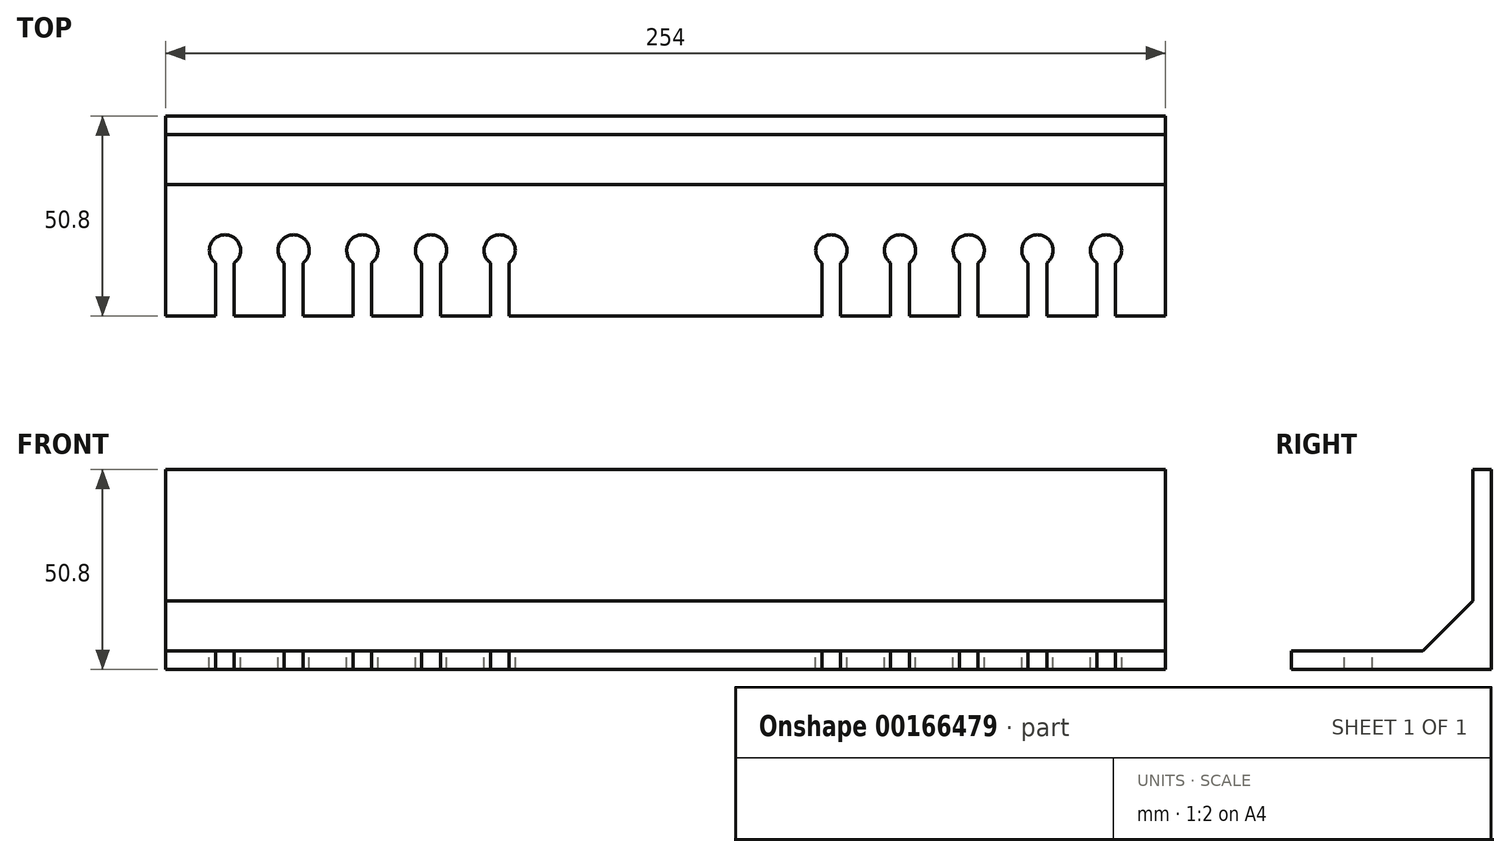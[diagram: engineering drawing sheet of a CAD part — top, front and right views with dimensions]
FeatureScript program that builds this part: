
annotation { "Feature Type Name" : "Feature", "Feature Type Description" : "" }
export const myFeature = defineFeature(function(context is Context, id is Id, definition is map)
    precondition{}
    {
        {
            var Q0;
            Q0=qCreatedBy(makeId("Right.planeOp"),FACE);
            var sketch = newSketch(context, id + "F0", { "sketchPlane" : qUnion([Q0])});
            skLineSegment(sketch, "E0.top", {"start": v(0, 46.05) * mm, "end": v(4.75, 46.05) * mm});
            skLineSegment(sketch, "E1.top", {"start": v(4.75, -4.75) * mm, "end": v(-46.05, -4.75) * mm});
            skLineSegment(sketch, "E1.right", {"start": v(-46.05, 0) * mm, "end": v(-46.05, -4.75) * mm});
            skLineSegment(sketch, "E2.trimOffspring", {"start": v(-12.7, 0) * mm, "end": v(-46.05, 0) * mm});
            skPoint(sketch, "E0.bottom.start.orphan", {"position": v(0, 0) * mm});
            skLineSegment(sketch, "E3", {"start": v(0, 46.05) * mm, "end": v(0, 12.7) * mm});
            skLineSegment(sketch, "E4", {"start": v(-12.7, 0) * mm, "end": v(0, 12.7) * mm});
            skLineSegment(sketch, "E5", {"start": v(4.75, 46.05) * mm, "end": v(4.75, -4.75) * mm});
            skSolve(sketch);
        }
        {
            var Q0;
            Q0 = qSketchRegion(id + "F0", true);
            extrude(context, id + "F1", {"entities" : qUnion([Q0]), "depth" : 254 * mm});
        }
        {
            var Q0;
            Q0=makeQuery(id+"F1.opExtrude","SWEPT_FACE",FACE,{"disambiguationData":[OSD([sQuery(id+"F0.wireOp",EDGE,"E2.trimOffspring")])]});
            var sketch = newSketch(context, id + "F2", { "sketchPlane" : qUnion([Q0])});
            skLineSegment(sketch, "E6.bottom", {"start": v(12.7, -46.05) * mm, "end": v(17.45, -46.05) * mm});
            skLineSegment(sketch, "E6.left", {"start": v(12.7, -46.05) * mm, "end": v(12.7, -33.35) * mm});
            skLineSegment(sketch, "E6.right", {"start": v(17.45, -46.05) * mm, "end": v(17.45, -33.35) * mm});
            skLineSegment(sketch, "E7.bottom", {"start": v(30.15, -46.05) * mm, "end": v(34.9, -46.05) * mm});
            skLineSegment(sketch, "E7.left", {"start": v(30.15, -46.05) * mm, "end": v(30.15, -33.35) * mm});
            skLineSegment(sketch, "E7.right", {"start": v(34.9, -46.05) * mm, "end": v(34.9, -33.35) * mm});
            skLineSegment(sketch, "E8.bottom", {"start": v(47.6, -46.05) * mm, "end": v(52.35, -46.05) * mm});
            skLineSegment(sketch, "E8.left", {"start": v(47.6, -46.05) * mm, "end": v(47.6, -33.35) * mm});
            skLineSegment(sketch, "E8.right", {"start": v(52.35, -46.05) * mm, "end": v(52.35, -33.35) * mm});
            skLineSegment(sketch, "E9.bottom", {"start": v(65.05, -46.05) * mm, "end": v(69.8, -46.05) * mm});
            skLineSegment(sketch, "E9.left", {"start": v(65.05, -46.05) * mm, "end": v(65.05, -33.35) * mm});
            skLineSegment(sketch, "E9.right", {"start": v(69.8, -46.05) * mm, "end": v(69.8, -33.35) * mm});
            skLineSegment(sketch, "E10.bottom", {"start": v(82.5, -46.05) * mm, "end": v(87.25, -46.05) * mm});
            skLineSegment(sketch, "E10.left", {"start": v(82.5, -46.05) * mm, "end": v(82.5, -33.35) * mm});
            skLineSegment(sketch, "E10.right", {"start": v(87.25, -46.05) * mm, "end": v(87.25, -33.35) * mm});
            skLineSegment(sketch, "E11.bottom", {"start": v(166.75, -46.05) * mm, "end": v(171.5, -46.05) * mm});
            skLineSegment(sketch, "E11.left", {"start": v(166.75, -46.05) * mm, "end": v(166.75, -33.35) * mm});
            skLineSegment(sketch, "E11.right", {"start": v(171.5, -46.05) * mm, "end": v(171.5, -33.35) * mm});
            skLineSegment(sketch, "E12.bottom", {"start": v(184.2, -46.05) * mm, "end": v(188.95, -46.05) * mm});
            skLineSegment(sketch, "E12.left", {"start": v(184.2, -46.05) * mm, "end": v(184.2, -33.35) * mm});
            skLineSegment(sketch, "E12.right", {"start": v(188.95, -46.05) * mm, "end": v(188.95, -33.35) * mm});
            skLineSegment(sketch, "E13.bottom", {"start": v(201.65, -46.05) * mm, "end": v(206.4, -46.05) * mm});
            skLineSegment(sketch, "E13.left", {"start": v(201.65, -46.05) * mm, "end": v(201.65, -33.35) * mm});
            skLineSegment(sketch, "E13.right", {"start": v(206.4, -46.05) * mm, "end": v(206.4, -33.35) * mm});
            skLineSegment(sketch, "E14.bottom", {"start": v(219.1, -46.05) * mm, "end": v(223.85, -46.05) * mm});
            skLineSegment(sketch, "E14.left", {"start": v(219.1, -46.05) * mm, "end": v(219.1, -33.35) * mm});
            skLineSegment(sketch, "E14.right", {"start": v(223.85, -46.05) * mm, "end": v(223.85, -33.35) * mm});
            skLineSegment(sketch, "E15.bottom", {"start": v(236.55, -46.05) * mm, "end": v(241.3, -46.05) * mm});
            skLineSegment(sketch, "E15.left", {"start": v(236.55, -46.05) * mm, "end": v(236.55, -33.35) * mm});
            skLineSegment(sketch, "E15.right", {"start": v(241.3, -46.05) * mm, "end": v(241.3, -33.35) * mm});
            skPoint(sketch, "E16.centerSnap0", {"position": v(15.07, -33.35) * mm});
            skArc(sketch, "E17", {"start": v(17.45, -32.56) * mm, "mid": v(15.07, -25.41) * mm, "end": v(12.7, -32.56) * mm});
            skArc(sketch, "E18", {"start": v(34.9, -32.56) * mm, "mid": v(32.52, -25.41) * mm, "end": v(30.15, -32.56) * mm});
            skPoint(sketch, "E18.centerSnap0", {"position": v(32.52, -33.35) * mm});
            skArc(sketch, "E19", {"start": v(52.35, -32.56) * mm, "mid": v(49.97, -25.41) * mm, "end": v(47.6, -32.56) * mm});
            skPoint(sketch, "E19.centerSnap0", {"position": v(49.97, -33.35) * mm});
            skArc(sketch, "E20", {"start": v(69.8, -32.56) * mm, "mid": v(67.42, -25.41) * mm, "end": v(65.05, -32.56) * mm});
            skPoint(sketch, "E20.centerSnap0", {"position": v(67.42, -33.35) * mm});
            skArc(sketch, "E21", {"start": v(87.25, -32.56) * mm, "mid": v(84.87, -25.41) * mm, "end": v(82.5, -32.56) * mm});
            skPoint(sketch, "E21.centerSnap0", {"position": v(84.87, -33.35) * mm});
            skArc(sketch, "E22", {"start": v(241.3, -32.56) * mm, "mid": v(238.93, -25.41) * mm, "end": v(236.55, -32.56) * mm});
            skPoint(sketch, "E22.centerSnap0", {"position": v(238.93, -33.35) * mm});
            skArc(sketch, "E23", {"start": v(223.85, -32.56) * mm, "mid": v(221.48, -25.41) * mm, "end": v(219.1, -32.56) * mm});
            skPoint(sketch, "E23.centerSnap0", {"position": v(221.48, -33.35) * mm});
            skArc(sketch, "E24", {"start": v(206.4, -32.56) * mm, "mid": v(204.03, -25.41) * mm, "end": v(201.65, -32.56) * mm});
            skPoint(sketch, "E24.centerSnap0", {"position": v(204.03, -33.35) * mm});
            skArc(sketch, "E25", {"start": v(188.95, -32.56) * mm, "mid": v(186.58, -25.41) * mm, "end": v(184.2, -32.56) * mm});
            skPoint(sketch, "E25.centerSnap0", {"position": v(186.58, -33.35) * mm});
            skArc(sketch, "E26", {"start": v(171.5, -32.56) * mm, "mid": v(169.13, -25.41) * mm, "end": v(166.75, -32.56) * mm});
            skPoint(sketch, "E26.centerSnap0", {"position": v(169.13, -33.35) * mm});
            skLineSegment(sketch, "E27", {"start": v(12.7, -33.35) * mm, "end": v(12.7, -32.56) * mm});
            skLineSegment(sketch, "E28", {"start": v(17.45, -33.35) * mm, "end": v(17.45, -32.56) * mm});
            skLineSegment(sketch, "E29", {"start": v(30.15, -33.35) * mm, "end": v(30.15, -32.56) * mm});
            skLineSegment(sketch, "E30", {"start": v(34.9, -33.35) * mm, "end": v(34.9, -32.56) * mm});
            skLineSegment(sketch, "E31", {"start": v(52.35, -33.35) * mm, "end": v(52.35, -32.56) * mm});
            skLineSegment(sketch, "E32", {"start": v(47.6, -33.35) * mm, "end": v(47.6, -32.56) * mm});
            skLineSegment(sketch, "E33", {"start": v(65.05, -33.35) * mm, "end": v(65.05, -32.56) * mm});
            skLineSegment(sketch, "E34", {"start": v(69.8, -33.35) * mm, "end": v(69.8, -32.56) * mm});
            skLineSegment(sketch, "E35", {"start": v(87.25, -33.35) * mm, "end": v(87.25, -32.56) * mm});
            skLineSegment(sketch, "E36", {"start": v(82.5, -33.35) * mm, "end": v(82.5, -32.56) * mm});
            skLineSegment(sketch, "E37", {"start": v(166.75, -33.35) * mm, "end": v(166.75, -32.56) * mm});
            skLineSegment(sketch, "E38", {"start": v(171.5, -33.35) * mm, "end": v(171.5, -32.56) * mm});
            skLineSegment(sketch, "E39", {"start": v(184.2, -33.35) * mm, "end": v(184.2, -32.56) * mm});
            skLineSegment(sketch, "E40", {"start": v(188.95, -33.35) * mm, "end": v(188.95, -32.56) * mm});
            skLineSegment(sketch, "E41", {"start": v(201.65, -33.35) * mm, "end": v(201.65, -32.56) * mm});
            skLineSegment(sketch, "E42", {"start": v(206.4, -33.35) * mm, "end": v(206.4, -32.56) * mm});
            skLineSegment(sketch, "E43", {"start": v(219.1, -33.35) * mm, "end": v(219.1, -32.56) * mm});
            skLineSegment(sketch, "E44", {"start": v(223.85, -33.35) * mm, "end": v(223.85, -32.56) * mm});
            skLineSegment(sketch, "E45", {"start": v(236.55, -33.35) * mm, "end": v(236.55, -32.56) * mm});
            skLineSegment(sketch, "E46", {"start": v(241.3, -33.35) * mm, "end": v(241.3, -32.56) * mm});
            skSolve(sketch);
        }
        {
            var Q0;
            Q0 = qSketchRegion(id + "F2", true);
            extrude(context, id + "F3", {"entities" : qUnion([Q0]), "operationType" : NewBodyOperationType.REMOVE, "oppositeDirection" : true, "depth" : 25.4 * mm});
        }
    });
